# Revit family: Скамейка стальная «Калипсо» без спинки Арт 14300
name_source: partatom
category: Антураж
revit_build: Autodesk Revit 2018 (Build: 20180423_1000(x64)
units: mm (PartAtom-declared; Revit-internal decimal feet)

## family parameters
Всегда вертикально = Да
Источник визуального образа = Геометрия семейства
На основе рабочей плоскости = Нет
Общий = Нет
При загрузке вырезать с полостями = Нет
Точка расчета площади = Нет

## types (2) — shared parameters
URL = https://hobbyka.ru
Артикул товара = Арт. 14300
Высота = 450 мм
Группа модели = Скамейки
Длина = 1810 мм
Изготовитель = ООО «Хоббика»
Изображение типоразмера = Скамейка стальная «Калипсо» без спинки Арт 14300.jpeg
Материал изделия = Сталь, дерево
Цвет каркаса = Сталь
Ширина = 780 мм

## per-type parameters (varying)
| type | Версия 1,8 м (лиственница) | Версия 1,8 м (сосна) | Описание | Цвет отделки |
| Версия 1,8 м (лиственница) | Да | Нет | Скамейка стальная «Калипсо» без спинки. Материал сидения из лиственницы | Лиственница |
| Версия 1,8 м (сосна) | Нет | Да | Скамейка стальная «Калипсо» без спинки. Материал сидения из сосны | Сосна |
